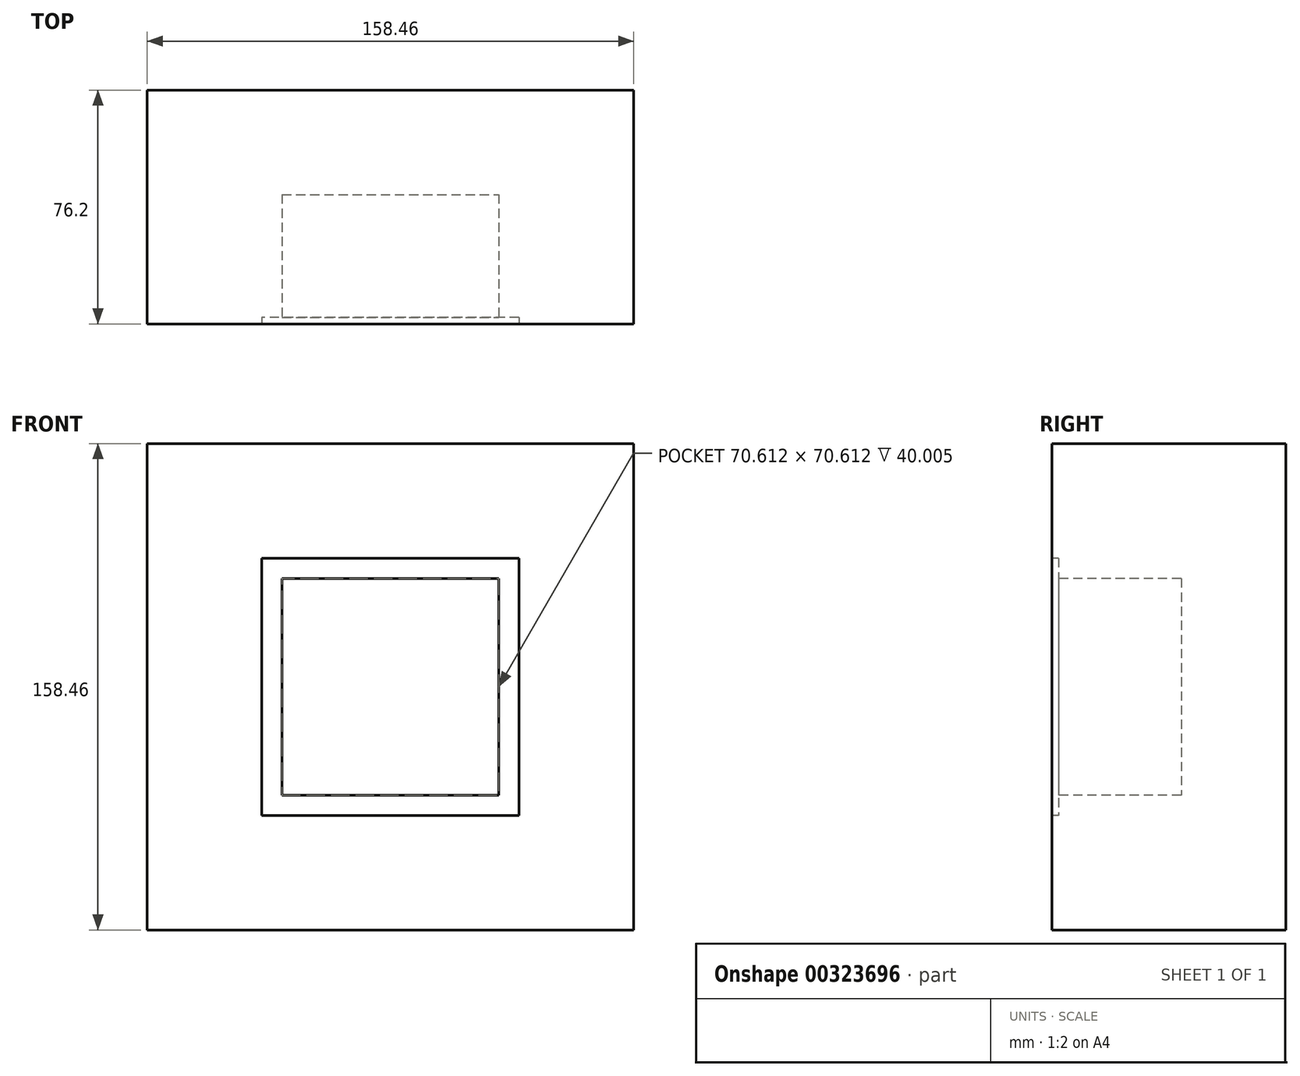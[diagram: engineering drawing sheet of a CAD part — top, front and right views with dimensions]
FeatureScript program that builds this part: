
annotation { "Feature Type Name" : "Feature", "Feature Type Description" : "" }
export const myFeature = defineFeature(function(context is Context, id is Id, definition is map)
    precondition{}
    {
        {
            var Q0;
            Q0=qCreatedBy(makeId("Front.planeOp"),FACE);
            var sketch = newSketch(context, id + "F0", { "sketchPlane" : qUnion([Q0])});
            skLineSegment(sketch, "E0.bottom", {"start": v(41.91, 41.9) * mm, "end": v(-41.9, 41.9) * mm});
            skLineSegment(sketch, "E0.top", {"start": v(41.91, -41.91) * mm, "end": v(-41.9, -41.91) * mm});
            skLineSegment(sketch, "E0.left", {"start": v(41.9, 41.9) * mm, "end": v(41.91, -41.91) * mm});
            skLineSegment(sketch, "E0.right", {"start": v(-41.9, 41.9) * mm, "end": v(-41.9, -41.91) * mm});
            skPoint(sketch, "E0.middle", {"position": v(0, 0) * mm});
            skLineSegment(sketch, "E1.bottom", {"start": v(-35.3, 35.3) * mm, "end": v(35.3, 35.3) * mm});
            skLineSegment(sketch, "E1.top", {"start": v(-35.3, -35.3) * mm, "end": v(35.3, -35.3) * mm});
            skLineSegment(sketch, "E1.left", {"start": v(-35.3, 35.3) * mm, "end": v(-35.3, -35.3) * mm});
            skLineSegment(sketch, "E1.right", {"start": v(35.3, 35.3) * mm, "end": v(35.3, -35.3) * mm});
            skLineSegment(sketch, "E2.bottom", {"start": v(-79.23, 79.23) * mm, "end": v(79.23, 79.23) * mm});
            skLineSegment(sketch, "E2.top", {"start": v(-79.23, -79.23) * mm, "end": v(79.23, -79.23) * mm});
            skLineSegment(sketch, "E2.left", {"start": v(-79.23, 79.23) * mm, "end": v(-79.23, -79.23) * mm});
            skLineSegment(sketch, "E2.right", {"start": v(79.23, 79.23) * mm, "end": v(79.23, -79.23) * mm});
            skSolve(sketch);
        }
        {
            var Q0;
            Q0=makeQuery(id+"F0.imprint","IMPRINT",FACE,{"disambiguationData":[TD([[makeQuery(id+"F0.imprint","IMPRINT",EDGE,{"derivedFrom":sQuery(id+"F0.wireOp",EDGE,"E0.bottom")}),1.0]])]});
            var sketch = newSketch(context, id + "F1", { "sketchPlane" : qUnion([Q0])});
            skLineSegment(sketch, "E3.bottom", {"start": v(-41.6, 41.6) * mm, "end": v(41.6, 41.6) * mm});
            skLineSegment(sketch, "E3.top", {"start": v(-41.6, -41.6) * mm, "end": v(41.6, -41.6) * mm});
            skLineSegment(sketch, "E3.left", {"start": v(-41.6, 41.6) * mm, "end": v(-41.6, -41.6) * mm});
            skLineSegment(sketch, "E3.right", {"start": v(41.6, 41.6) * mm, "end": v(41.6, -41.6) * mm});
            skPoint(sketch, "E3.middle", {"position": v(0, 0) * mm});
            skLineSegment(sketch, "E4.bottom", {"start": v(29.72, 29.72) * mm, "end": v(-29.72, 29.72) * mm});
            skLineSegment(sketch, "E4.top", {"start": v(29.72, -29.72) * mm, "end": v(-29.72, -29.72) * mm});
            skLineSegment(sketch, "E4.left", {"start": v(29.72, 29.72) * mm, "end": v(29.72, -29.72) * mm});
            skLineSegment(sketch, "E4.right", {"start": v(-29.72, 29.72) * mm, "end": v(-29.72, -29.72) * mm});
            skCircle(sketch, "E5", {"center": v(0, 29.72) * mm, "radius": 5.08 * mm});
            skCircle(sketch, "E6", {"center": v(0, 29.72) * mm, "radius": 2.22 * mm});
            skCircle(sketch, "E7.1.0", {"center": v(29.72, 0) * mm, "radius": 5.08 * mm});
            skCircle(sketch, "E7.1.1", {"center": v(29.72, 0) * mm, "radius": 2.22 * mm});
            skCircle(sketch, "E7.2.0", {"center": v(0, -29.72) * mm, "radius": 5.08 * mm});
            skCircle(sketch, "E7.2.1", {"center": v(0, -29.72) * mm, "radius": 2.22 * mm});
            skCircle(sketch, "E7.3.0", {"center": v(-29.72, 0) * mm, "radius": 5.08 * mm});
            skCircle(sketch, "E7.3.1", {"center": v(-29.72, 0) * mm, "radius": 2.22 * mm});
            skLineSegment(sketch, "E7.anchor1", {"start": v(0, 0) * mm, "end": v(0, 29.72) * mm, "construction": true});
            skLineSegment(sketch, "E7.anchor2", {"start": v(0, 0) * mm, "end": v(-29.72, 0) * mm, "construction": true});
            skSolve(sketch);
        }
        {
            var Q0;
            Q0=makeQuery(id+"F1.imprint","IMPRINT",FACE,{"disambiguationData":[TD([[makeQuery(id+"F1.imprint","IMPRINT",EDGE,{"derivedFrom":sQuery(id+"F1.wireOp",EDGE,"E3.bottom")}),-1.0]])]});
            var Q1;
            Q1=makeQuery(id+"F1.imprint","IMPRINT",FACE,{"disambiguationData":[TD([[makeQuery(id+"F1.imprint","IMPRINT",EDGE,{"derivedFrom":makeQuery(id+"F0.imprint","IMPRINT",EDGE,{"derivedFrom":sQuery(id+"F0.wireOp",EDGE,"E1.bottom")})}),-1.0]])]});
            var Q2;
            {var subQ0=sQuery(id+"F1.wireOp",EDGE,"E7.3.0");var subQ1=sQuery(id+"F1.wireOp",EDGE,"E4.right");var subQ2=makeQuery(id+"F1.imprint","INTERSECT",VERTEX,{"disambiguationData":[OD(0.0)],"derivedFrom":[subQ1,subQ0]});Q2=makeQuery(id+"F1.imprint","IMPRINT",FACE,{"disambiguationData":[TD([[makeQuery(id+"F1.imprint","IMPRINT",EDGE,{"disambiguationData":[TD([[subQ2,-1.0]])],"derivedFrom":subQ1}),-1.0]])]});}
            var Q3;
            {var subQ0=sQuery(id+"F1.wireOp",EDGE,"E7.3.0");var subQ1=sQuery(id+"F1.wireOp",EDGE,"E4.right");var subQ2=makeQuery(id+"F1.imprint","INTERSECT",VERTEX,{"disambiguationData":[OD(0.0)],"derivedFrom":[subQ1,subQ0]});Q3=makeQuery(id+"F1.imprint","IMPRINT",FACE,{"disambiguationData":[TD([[makeQuery(id+"F1.imprint","IMPRINT",EDGE,{"disambiguationData":[TD([[subQ2,-1.0]])],"derivedFrom":subQ1}),1.0]])]});}
            var Q4;
            {var subQ0=sQuery(id+"F1.wireOp",EDGE,"E5");var subQ1=sQuery(id+"F1.wireOp",EDGE,"E4.bottom");var subQ2=makeQuery(id+"F1.imprint","INTERSECT",VERTEX,{"disambiguationData":[OD(0.0)],"derivedFrom":[subQ1,subQ0]});Q4=makeQuery(id+"F1.imprint","IMPRINT",FACE,{"disambiguationData":[TD([[makeQuery(id+"F1.imprint","IMPRINT",EDGE,{"disambiguationData":[TD([[subQ2,-1.0]])],"derivedFrom":subQ1}),1.0]])]});}
            var Q5;
            {var subQ0=sQuery(id+"F1.wireOp",EDGE,"E5");var subQ1=sQuery(id+"F1.wireOp",EDGE,"E4.bottom");var subQ2=makeQuery(id+"F1.imprint","INTERSECT",VERTEX,{"disambiguationData":[OD(0.0)],"derivedFrom":[subQ1,subQ0]});Q5=makeQuery(id+"F1.imprint","IMPRINT",FACE,{"disambiguationData":[TD([[makeQuery(id+"F1.imprint","IMPRINT",EDGE,{"disambiguationData":[TD([[subQ2,-1.0]])],"derivedFrom":subQ1}),-1.0]])]});}
            var Q6;
            {var subQ0=sQuery(id+"F1.wireOp",EDGE,"E7.1.0");var subQ1=sQuery(id+"F1.wireOp",EDGE,"E4.left");var subQ2=makeQuery(id+"F1.imprint","INTERSECT",VERTEX,{"disambiguationData":[OD(0.0)],"derivedFrom":[subQ1,subQ0]});Q6=makeQuery(id+"F1.imprint","IMPRINT",FACE,{"disambiguationData":[TD([[makeQuery(id+"F1.imprint","IMPRINT",EDGE,{"disambiguationData":[TD([[subQ2,-1.0]])],"derivedFrom":subQ1}),-1.0]])]});}
            var Q7;
            {var subQ0=sQuery(id+"F1.wireOp",EDGE,"E7.1.0");var subQ1=sQuery(id+"F1.wireOp",EDGE,"E4.left");var subQ2=makeQuery(id+"F1.imprint","INTERSECT",VERTEX,{"disambiguationData":[OD(0.0)],"derivedFrom":[subQ1,subQ0]});Q7=makeQuery(id+"F1.imprint","IMPRINT",FACE,{"disambiguationData":[TD([[makeQuery(id+"F1.imprint","IMPRINT",EDGE,{"disambiguationData":[TD([[subQ2,-1.0]])],"derivedFrom":subQ1}),1.0]])]});}
            var Q8;
            {var subQ0=sQuery(id+"F1.wireOp",EDGE,"E7.2.0");var subQ1=sQuery(id+"F1.wireOp",EDGE,"E4.top");var subQ2=makeQuery(id+"F1.imprint","INTERSECT",VERTEX,{"disambiguationData":[OD(0.0)],"derivedFrom":[subQ1,subQ0]});Q8=makeQuery(id+"F1.imprint","IMPRINT",FACE,{"disambiguationData":[TD([[makeQuery(id+"F1.imprint","IMPRINT",EDGE,{"disambiguationData":[TD([[subQ2,-1.0]])],"derivedFrom":subQ1}),1.0]])]});}
            var Q9;
            {var subQ0=sQuery(id+"F1.wireOp",EDGE,"E7.2.0");var subQ1=sQuery(id+"F1.wireOp",EDGE,"E4.top");var subQ2=makeQuery(id+"F1.imprint","INTERSECT",VERTEX,{"disambiguationData":[OD(0.0)],"derivedFrom":[subQ1,subQ0]});Q9=makeQuery(id+"F1.imprint","IMPRINT",FACE,{"disambiguationData":[TD([[makeQuery(id+"F1.imprint","IMPRINT",EDGE,{"disambiguationData":[TD([[subQ2,-1.0]])],"derivedFrom":subQ1}),-1.0]])]});}
            extrude(context, id + "F2", {"entities" : qUnion([Q0, Q1, Q2, Q3, Q4, Q5, Q6, Q7, Q8, Q9]), "oppositeDirection" : true, "depth" : 2.16 * mm});
        }
        {
            var Q0;
            Q0=makeQuery(id+"F0.imprint","IMPRINT",FACE,{"disambiguationData":[TD([[makeQuery(id+"F0.imprint","IMPRINT",EDGE,{"derivedFrom":sQuery(id+"F0.wireOp",EDGE,"E0.bottom")}),-1.0]])]});
            var Q1;
            Q1=makeQuery(id+"F0.imprint","IMPRINT",FACE,{"disambiguationData":[TD([[makeQuery(id+"F0.imprint","IMPRINT",EDGE,{"derivedFrom":sQuery(id+"F0.wireOp",EDGE,"E1.bottom")}),-1.0]])]});
            var Q2;
            Q2=makeQuery(id+"F0.imprint","IMPRINT",FACE,{"disambiguationData":[TD([[makeQuery(id+"F0.imprint","IMPRINT",EDGE,{"derivedFrom":sQuery(id+"F0.wireOp",EDGE,"E0.bottom")}),1.0]])]});
            extrude(context, id + "F3", {"entities" : qUnion([Q0, Q1, Q2]), "oppositeDirection" : true, "depth" : 76.2 * mm});
        }
        {
            var Q0;
            Q0=makeQuery(id+"F0.imprint","IMPRINT",FACE,{"disambiguationData":[TD([[makeQuery(id+"F0.imprint","IMPRINT",EDGE,{"derivedFrom":sQuery(id+"F0.wireOp",EDGE,"E0.bottom")}),1.0]])]});
            var Q1;
            Q1=makeQuery(id+"F0.imprint","IMPRINT",FACE,{"disambiguationData":[TD([[makeQuery(id+"F0.imprint","IMPRINT",EDGE,{"derivedFrom":sQuery(id+"F0.wireOp",EDGE,"E1.bottom")}),-1.0]])]});
            extrude(context, id + "F4", {"entities" : qUnion([Q0, Q1]), "operationType" : NewBodyOperationType.REMOVE, "oppositeDirection" : true, "depth" : 2.16 * mm});
        }
        {
            var Q0;
            Q0=makeQuery(id+"F0.imprint","IMPRINT",FACE,{"disambiguationData":[TD([[makeQuery(id+"F0.imprint","IMPRINT",EDGE,{"derivedFrom":sQuery(id+"F0.wireOp",EDGE,"E1.bottom")}),-1.0]])]});
            extrude(context, id + "F5", {"entities" : qUnion([Q0]), "operationType" : NewBodyOperationType.REMOVE, "oppositeDirection" : true, "depth" : 42.16 * mm});
        }
    });
